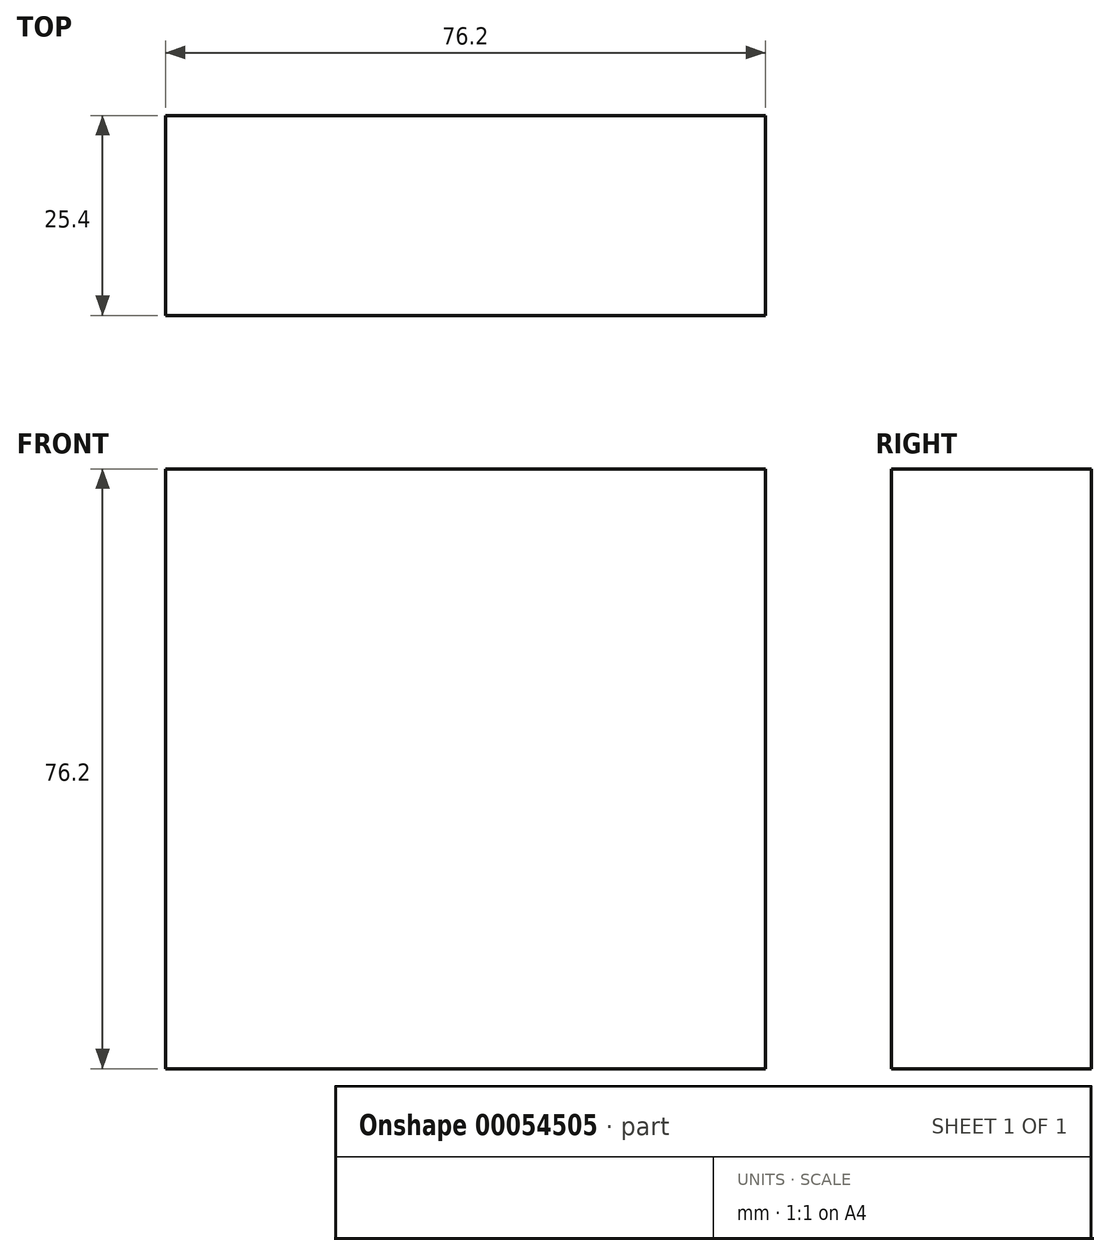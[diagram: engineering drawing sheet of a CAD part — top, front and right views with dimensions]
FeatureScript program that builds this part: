
annotation { "Feature Type Name" : "Feature", "Feature Type Description" : "" }
export const myFeature = defineFeature(function(context is Context, id is Id, definition is map)
    precondition{}
    {
        {
            var Q0;
            Q0=qCreatedBy(makeId("Front.planeOp"),FACE);
            var sketch = newSketch(context, id + "F0", { "sketchPlane" : qUnion([Q0])});
            skLineSegment(sketch, "E0.bottom", {"start": v(-59.4, 71.34) * mm, "end": v(16.8, 71.34) * mm});
            skLineSegment(sketch, "E0.top", {"start": v(-59.4, -4.86) * mm, "end": v(16.8, -4.86) * mm});
            skLineSegment(sketch, "E0.left", {"start": v(-59.4, 71.34) * mm, "end": v(-59.4, -4.86) * mm});
            skLineSegment(sketch, "E0.right", {"start": v(16.8, 71.34) * mm, "end": v(16.8, -4.86) * mm});
            skSolve(sketch);
        }
        {
            var Q0;
            Q0=makeQuery(id+"F0.imprint","IMPRINT",FACE,{"disambiguationData":[TD([[makeQuery(id+"F0.imprint","IMPRINT",EDGE,{"derivedFrom":sQuery(id+"F0.wireOp",EDGE,"E0.bottom")}),-1.0]])]});
            extrude(context, id + "F1", {"entities" : qUnion([Q0]), "depth" : 25.4 * mm});
        }
    });
